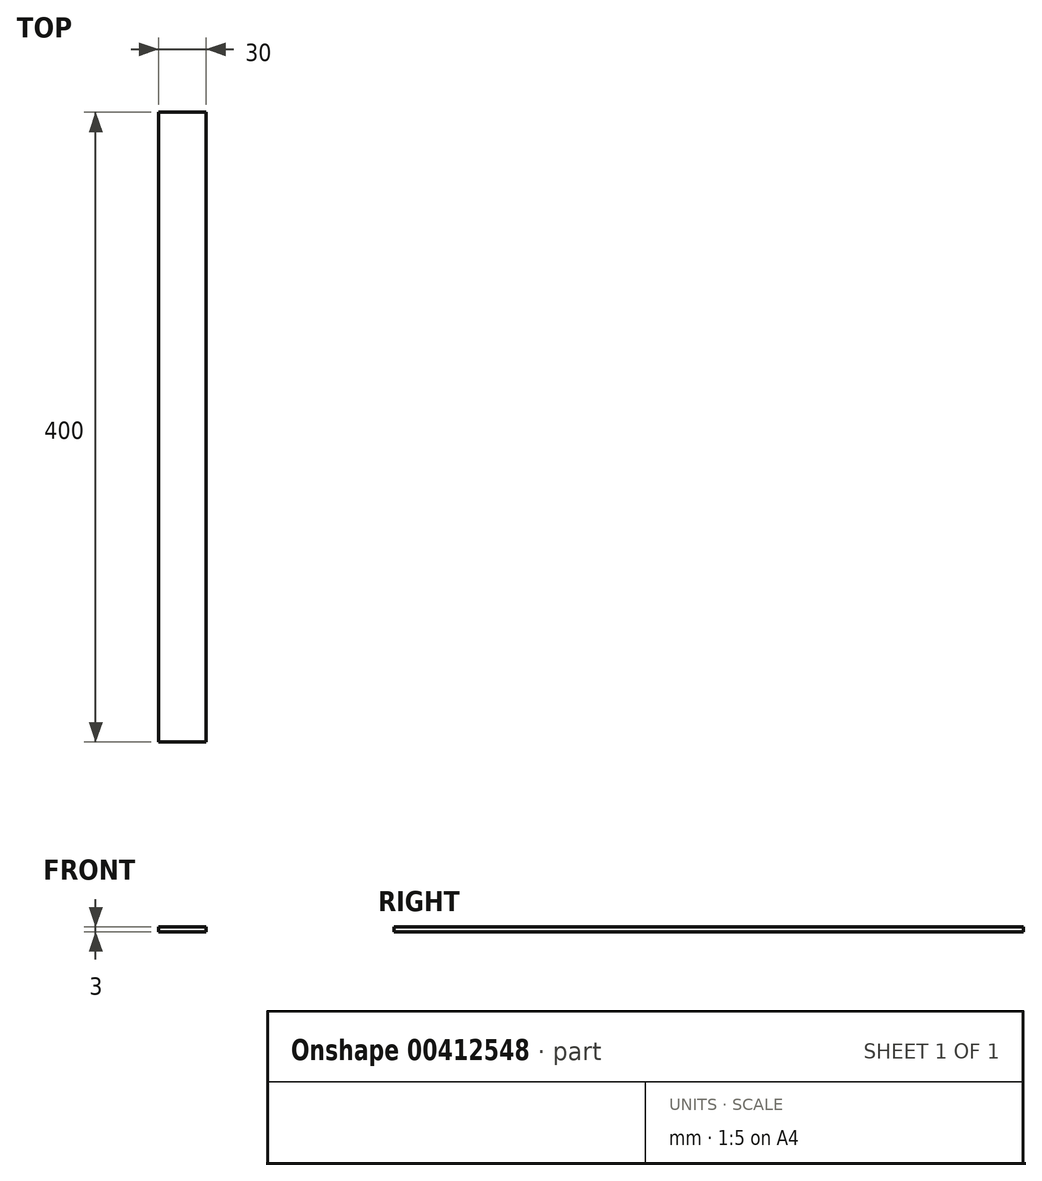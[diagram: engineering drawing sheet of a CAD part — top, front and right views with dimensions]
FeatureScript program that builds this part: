
annotation { "Feature Type Name" : "Feature", "Feature Type Description" : "" }
export const myFeature = defineFeature(function(context is Context, id is Id, definition is map)
    precondition{}
    {
        {
            var Q0;
            Q0=qCreatedBy(makeId("Top.planeOp"),FACE);
            var sketch = newSketch(context, id + "F0", { "sketchPlane" : qUnion([Q0])});
            skLineSegment(sketch, "E0.bottom", {"start": v(-62.38, 352.5) * mm, "end": v(-32.38, 352.5) * mm});
            skLineSegment(sketch, "E0.top", {"start": v(-62.38, -47.5) * mm, "end": v(-32.38, -47.5) * mm});
            skLineSegment(sketch, "E0.left", {"start": v(-62.38, 352.5) * mm, "end": v(-62.38, -47.5) * mm});
            skLineSegment(sketch, "E0.right", {"start": v(-32.38, 352.5) * mm, "end": v(-32.38, -47.5) * mm});
            skSolve(sketch);
        }
        {
            var Q0;
            Q0 = qSketchRegion(id + "F0", true);
            extrude(context, id + "F1", {"entities" : qUnion([Q0]), "depth" : 3 * mm});
        }
    });
